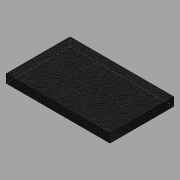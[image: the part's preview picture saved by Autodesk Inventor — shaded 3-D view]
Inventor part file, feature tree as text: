
AUTODESK INVENTOR PART (.ipt)
format: ipt  version: 2015 (Build 190159000, 159)  size: 82,944 bytes
history: native  units: in
note: dims shown in document units (in); Inventor stores cm internally (conversion verified against a paired STEP export)
features: other x3, sketch x1
ambient origin geometry x8: Origin, YZ Plane, XZ Plane, XY Plane, X Axis, Y Axis, Z Axis, Center Point
bodies: Solid1 (feature_tree)
feature tree (4):
  other  "bateria.ipt"
  other  "Solid1::bateria.ipt"
  other  "TaggingFeature1"
  sketch  "Sketch1"  dims[d0=0.3937in]
